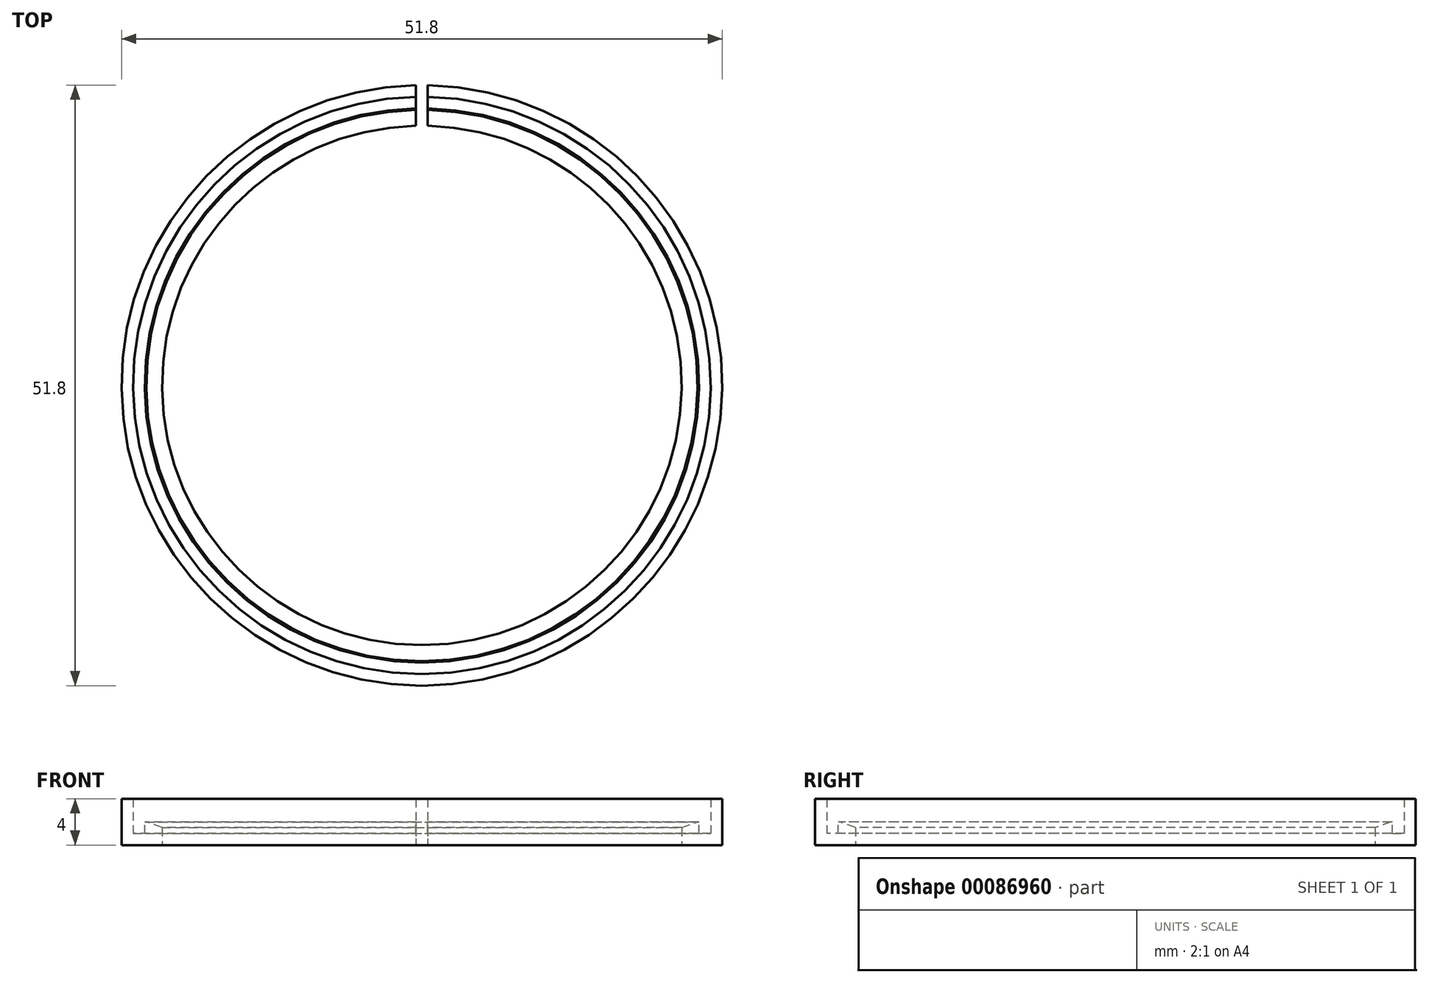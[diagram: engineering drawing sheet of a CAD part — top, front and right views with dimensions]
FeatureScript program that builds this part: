
annotation { "Feature Type Name" : "Feature", "Feature Type Description" : "" }
export const myFeature = defineFeature(function(context is Context, id is Id, definition is map)
    precondition{}
    {
        {
            var Q0;
            Q0=qCreatedBy(makeId("Top.planeOp"),FACE);
            var sketch = newSketch(context, id + "F0", { "sketchPlane" : qUnion([Q0])});
            skCircle(sketch, "E0", {"center": v(0, 0) * mm, "radius": 25.9 * mm});
            skCircle(sketch, "E1", {"center": v(0, 0) * mm, "radius": 22.4 * mm});
            skSolve(sketch);
        }
        {
            var Q0;
            Q0=makeQuery(id+"F0.imprint","IMPRINT",FACE,{"disambiguationData":[TD([[makeQuery(id+"F0.imprint","IMPRINT",EDGE,{"derivedFrom":sQuery(id+"F0.wireOp",EDGE,"E0")}),1.0]])]});
            extrude(context, id + "F1", {"entities" : qUnion([Q0]), "depth" : 2 * mm});
        }
        {
            var Q0;
            Q0=makeQuery(id+"F1.opExtrude","CAP_FACE",FACE,{"disambiguationData":[OSD([sQuery(id+"F0.wireOp",EDGE,"E0"),sQuery(id+"F0.wireOp",EDGE,"E1")])],"isStart":false});
            var sketch = newSketch(context, id + "F2", { "sketchPlane" : qUnion([Q0])});
            skCircle(sketch, "E2", {"center": v(0, 0) * mm, "radius": 24.9 * mm});
            skCircle(sketch, "E3.0", {"center": v(0, 0) * mm, "radius": 25.9 * mm});
            skSolve(sketch);
        }
        {
            var Q0;
            Q0 = qSketchRegion(id + "F2", true);
            extrude(context, id + "F3", {"entities" : qUnion([Q0]), "operationType" : NewBodyOperationType.ADD, "depth" : 2 * mm});
        }
        {
            var Q0;
            Q0=makeQuery(id+"F1.opExtrude","CAP_FACE",FACE,{"disambiguationData":[OSD([sQuery(id+"F0.wireOp",EDGE,"E0"),sQuery(id+"F0.wireOp",EDGE,"E1")])],"isStart":true});
            var sketch = newSketch(context, id + "F4", { "sketchPlane" : qUnion([Q0])});
            skLineSegment(sketch, "E4.bottom", {"start": v(-0.5, -20) * mm, "end": v(0.5, -20) * mm});
            skLineSegment(sketch, "E4.top", {"start": v(-0.5, -30) * mm, "end": v(0.5, -30) * mm});
            skLineSegment(sketch, "E4.left", {"start": v(-0.5, -20) * mm, "end": v(-0.5, -30) * mm});
            skLineSegment(sketch, "E4.right", {"start": v(0.5, -20) * mm, "end": v(0.5, -30) * mm});
            skPoint(sketch, "E4.middle", {"position": v(0, -25) * mm});
            skSolve(sketch);
        }
        {
            var Q0;
            Q0 = qSketchRegion(id + "F4", true);
            extrude(context, id + "F5", {"entities" : qUnion([Q0]), "operationType" : NewBodyOperationType.REMOVE, "oppositeDirection" : true, "depth" : 25 * mm});
        }
        {
            var Q0;
            Q0=makeQuery(id+"F1.opExtrude","CAP_FACE",FACE,{"disambiguationData":[OSD([sQuery(id+"F0.wireOp",EDGE,"E0"),sQuery(id+"F0.wireOp",EDGE,"E1")])],"isStart":false});
            var sketch = newSketch(context, id + "F6", { "sketchPlane" : qUnion([Q0])});
            skArc(sketch, "E5.0", {"start": v(-0.5, 24.9) * mm, "mid": v(0, -24.9) * mm, "end": v(0.5, 24.9) * mm, "construction": true});
            skCircle(sketch, "E6", {"center": v(0, 0) * mm, "radius": 24.9 * mm});
            skCircle(sketch, "E7", {"center": v(0, 0) * mm, "radius": 23.9 * mm});
            skSolve(sketch);
        }
        {
            var Q0;
            Q0 = qSketchRegion(id + "F6", true);
            extrude(context, id + "F7", {"entities" : qUnion([Q0]), "operationType" : NewBodyOperationType.REMOVE, "oppositeDirection" : true, "depth" : 1 * mm});
        }
        {
            var Q0;
            Q0=makeQuery(id+"F1.opExtrude","CAP_EDGE",EDGE,{"disambiguationData":[OSD([sQuery(id+"F0.wireOp",EDGE,"E1")])],"isStart":false});
            chamfer(context, id + "F8", {"entities" : qUnion([Q0]), "chamferType" : ChamferType.OFFSET_ANGLE, "width" : 0.5 * mm, "oppositeDirection" : false, "angle" : 70 * degree, "tangentPropagation" : true});
        }
    });
